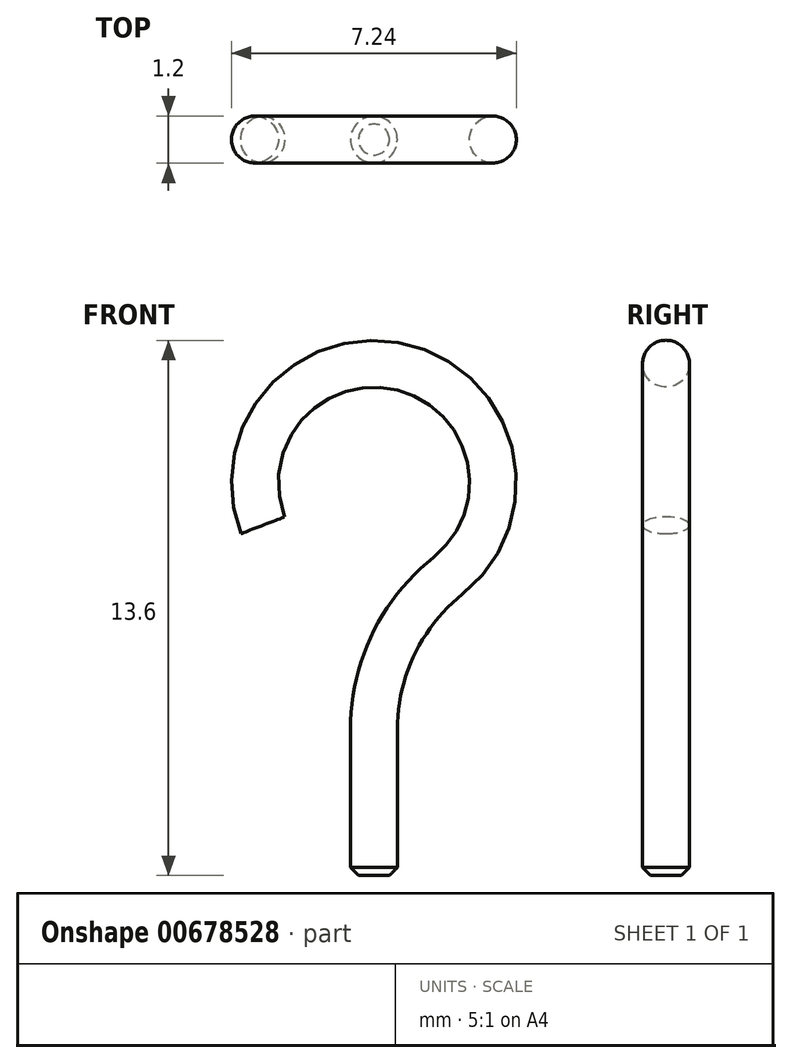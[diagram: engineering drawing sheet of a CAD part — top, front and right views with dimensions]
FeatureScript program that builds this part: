
annotation { "Feature Type Name" : "Feature", "Feature Type Description" : "" }
export const myFeature = defineFeature(function(context is Context, id is Id, definition is map)
    precondition{}
    {
        {
            var Q0;
            Q0=qCreatedBy(makeId("Front.planeOp"),FACE);
            var sketch = newSketch(context, id + "F0", { "sketchPlane" : qUnion([Q0])});
            skArc(sketch, "E0", {"start": v(1.88, 7.62) * mm, "mid": v(0.8, 12.9) * mm, "end": v(-2.82, 8.9) * mm});
            skLineSegment(sketch, "E1", {"start": v(0, 3.7) * mm, "end": v(0, 0) * mm});
            skPoint(sketch, "E2.visualSharp", {"position": v(0, 6.96) * mm});
            skArc(sketch, "E2.filletArc", {"start": v(1.88, 7.62) * mm, "mid": v(0.5, 5.88) * mm, "end": v(0, 3.7) * mm});
            skSolve(sketch);
        }
        {
            var Q0;
            Q0=qCreatedBy(makeId("Top.planeOp"),FACE);
            var sketch = newSketch(context, id + "F1", { "sketchPlane" : qUnion([Q0])});
            skCircle(sketch, "E3", {"center": v(0, 0) * mm, "radius": 0.6 * mm});
            skSolve(sketch);
        }
        {
            var Q0;
            Q0=makeQuery(id+"F1.imprint","IMPRINT",FACE,{"disambiguationData":[TD([[makeQuery(id+"F1.imprint","IMPRINT",EDGE,{"derivedFrom":sQuery(id+"F1.wireOp",EDGE,"E3")}),1.0]])]});
            var Q1;
            Q1=sQuery(id+"F0.wireOp",EDGE,"E1");
            var Q2;
            Q2=sQuery(id+"F0.wireOp",EDGE,"E2.filletArc");
            var Q3;
            Q3=sQuery(id+"F0.wireOp",EDGE,"E0");
            sweep(context, id + "F2", {"profiles" : qUnion([Q0]), "path" : qUnion([Q1, Q2, Q3])});
        }
        {
            var Q0;
            Q0=makeQuery(id+"F2.opSweep","CAP_EDGE",EDGE,{"disambiguationData":[OSD([sQuery(id+"F0.wireOp",VERTEX,"E1.end"),sQuery(id+"F1.wireOp",EDGE,"E3")])],"isStart":true});
            chamfer(context, id + "F3", {"entities" : qUnion([Q0]), "width" : 0.2 * mm, "tangentPropagation" : true});
        }
    });
